# Revit family: Vent Valve Assembly-JCI_Sapphire_Plus-(70bar)Novec1230
name_source: partatom
category: Specialty Equipment
revit_build: Autodesk Revit 2017 (Build: 20171027_0315(x64)
units: mm (PartAtom-declared; Revit-internal decimal feet)

## family parameters
Always vertical = No
Cut with Voids When Loaded = No
OmniClass Number = 23.29.33.13.11
Part Type = Normal
Room Calculation Point = No
Round Connector Dimension = Use Diameter
Shared = No
Work Plane-Based = No

## types (1)
- Vent Valve Assembly 3/4" NPT
    Date Modified = YYYY/MM/DD
    Description = Vent Valve Assembly
    Discharge Flow = 0 GPM
    Equipment Abbreviation = --
    Family Version = 1.0
    Fire Suppression Agent = 3M NOVEC 1230 Fire Protection Fluid
    Length = 47.5 mm
    Limit Switch Material = JCI - Iron - Gray
    Manufacturer = Johnson Controls, Inc.
    Materials = JCI - Metal - Stainless Steel - Satin
    Model = 302700014
    Model Disclaimer = For More Information Contact  JOHNSON CONTROLS
    Operating Temperature = 122 °F
    Product Documentation Link = http://www.sapphireplus.com
    Product Material = JCI - Iron - Gray ; JCI - Metal - Stainless Steel - Satin
    Product Page URL = http://www.sapphireplus.com
    URL = http://www.sapphireplus.com
    Weight = 5.10 lbf

## geometry (parser evidence)
native form markers: Sweep x2
no freeform markers — native parametric forms only
